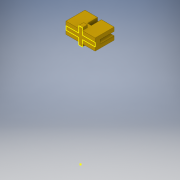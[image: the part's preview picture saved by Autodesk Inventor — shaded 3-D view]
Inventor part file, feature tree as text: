
AUTODESK INVENTOR PART (.ipt)
format: ipt  version: 2019 (Build 230136000, 136)  size: 359,936 bytes
history: native  units: mm
features: reference x6, projected_geometry x6, sketch x4, extrude x3, other x3
ambient origin geometry x8: Origin, YZ Plane, XZ Plane, XY Plane, X Axis, Y Axis, Z Axis, Center Point
bodies: Solid1 (feature_tree)
feature tree (22):
  extrude  "Extrusion1"  Depth=10.0mm
  sketch  "Sketch2"  dims[d2=4.0mm d3=0.0mm d4=3.0mm]
  extrude  "Extrusion2"  Depth=3.0mm
  extrude  "Extrusion3"  Depth=15.0mm TaperAngle=0.0deg
  sketch  "Sketch1"  dims[d0=10.0mm d1=10.0mm]
  reference  "Reference1"
  reference  "Reference2"
  reference  "Reference3"
  reference  "Reference4"
  reference  "Reference5"
  reference  "Reference6"
  projected_geometry  "Projected Loop1"
  sketch  "Sketch3"  dims[d5=3.0mm d6=15.0mm d7=0.0mm]
  sketch  "Sketch4"  dims[d8=3.0mm d9=3.0mm d10=3.0mm d11=3.0mm d12=3.0mm d13=0.0mm d14=3.0mm d15=3.0mm]
  projected_geometry  "Projected Loop2"
  projected_geometry  "Projected Loop3"
  projected_geometry  "Projected Loop4"
  projected_geometry  "Projected Loop5"
  projected_geometry  "Projected Loop6"
  other  "Assembly1"
  other  "Base v6 - 175:2"
  other  "Base v6 - 175:1"
